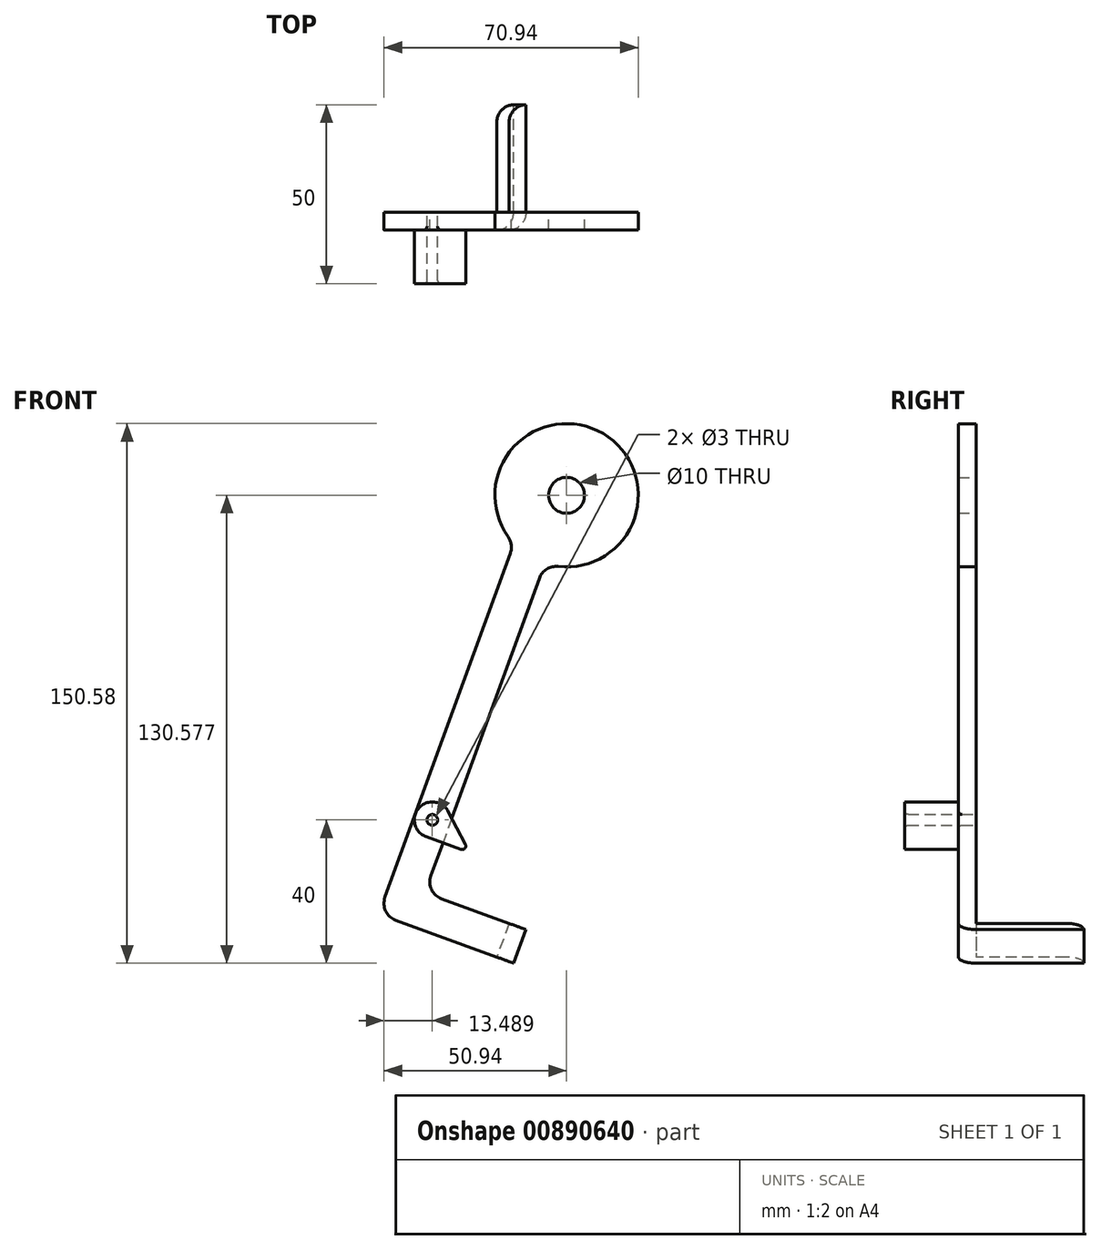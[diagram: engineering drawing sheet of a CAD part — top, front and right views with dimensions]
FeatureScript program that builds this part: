
annotation { "Feature Type Name" : "Feature", "Feature Type Description" : "" }
export const myFeature = defineFeature(function(context is Context, id is Id, definition is map)
    precondition{}
    {
        {
            var Q0;
            Q0=qCreatedBy(makeId("Front.planeOp"),FACE);
            var sketch = newSketch(context, id + "F0", { "sketchPlane" : qUnion([Q0])});
            skCircle(sketch, "E0", {"center": v(0, 33.82) * mm, "radius": 5 * mm});
            skLineSegment(sketch, "E1", {"start": v(0, 70.54) * mm, "end": v(0, -41.15) * mm, "construction": true});
            skLineSegment(sketch, "E2", {"start": v(-33.6, -60.82) * mm, "end": v(-32.58, -58) * mm});
            skLineSegment(sketch, "E3", {"start": v(-32.58, -58) * mm, "end": v(-32.58, -58) * mm});
            skCircle(sketch, "E4", {"center": v(0, 33.82) * mm, "radius": 20 * mm});
            skLineSegment(sketch, "E5", {"start": v(-6.1, 14.77) * mm, "end": v(-32.58, -58) * mm});
            skLineSegment(sketch, "E6", {"start": v(-14.73, 20.29) * mm, "end": v(-42.32, -55.52) * mm});
            skLineSegment(sketch, "E7", {"start": v(-14.73, 20.29) * mm, "end": v(-52.35, -83.08) * mm});
            skLineSegment(sketch, "E8", {"start": v(-6.1, 14.77) * mm, "end": v(-42.95, -86.5) * mm});
            skLineSegment(sketch, "E9", {"start": v(-52.35, -83.08) * mm, "end": v(-42.95, -86.5) * mm});
            skLineSegment(sketch, "E10", {"start": v(-42.95, -86.5) * mm, "end": v(-14.76, -96.76) * mm});
            skLineSegment(sketch, "E11", {"start": v(-14.76, -96.76) * mm, "end": v(-11.34, -87.36) * mm});
            skLineSegment(sketch, "E12", {"start": v(-11.34, -87.36) * mm, "end": v(-39.53, -77.1) * mm});
            skLineSegment(sketch, "E13", {"start": v(-16.04, -85.65) * mm, "end": v(-19.46, -95.05) * mm});
            skCircle(sketch, "E14", {"center": v(-37.45, -56.76) * mm, "radius": 5 * mm});
            skCircle(sketch, "E15", {"center": v(-37.45, -56.76) * mm, "radius": 1.5 * mm});
            skLineSegment(sketch, "E16", {"start": v(-37.45, -56.76) * mm, "end": v(-36.77, -54.88) * mm, "construction": true});
            skLineSegment(sketch, "E17", {"start": v(-37.45, -56.76) * mm, "end": v(-38.14, -58.64) * mm, "construction": true});
            skLineSegment(sketch, "E18", {"start": v(-36.77, -54.88) * mm, "end": v(-32.07, -56.6) * mm, "construction": true});
            skLineSegment(sketch, "E19", {"start": v(-38.14, -58.64) * mm, "end": v(-33.44, -60.35) * mm, "construction": true});
            skLineSegment(sketch, "E20", {"start": v(-33.83, -60.2) * mm, "end": v(-33.44, -60.35) * mm});
            skLineSegment(sketch, "E21", {"start": v(-32.46, -56.45) * mm, "end": v(-32.07, -56.6) * mm});
            skLineSegment(sketch, "E22", {"start": v(-32.07, -56.6) * mm, "end": v(-24.55, -59.33) * mm});
            skLineSegment(sketch, "E23", {"start": v(-33.44, -60.35) * mm, "end": v(-25.92, -63.09) * mm});
            skLineSegment(sketch, "E24", {"start": v(-24.55, -59.33) * mm, "end": v(-25.92, -63.09) * mm});
            skLineSegment(sketch, "E25", {"start": v(-32.07, -56.6) * mm, "end": v(-30.66, -57.1) * mm});
            skLineSegment(sketch, "E26", {"start": v(-30.66, -57.1) * mm, "end": v(-32.03, -60.86) * mm});
            skLineSegment(sketch, "E27", {"start": v(-30.66, -57.1) * mm, "end": v(-25.92, -63.09) * mm});
            skSolve(sketch);
        }
        {
            var Q0;
            Q0=makeQuery(id+"F0.imprint","IMPRINT",FACE,{"disambiguationData":[TD([[makeQuery(id+"F0.imprint","IMPRINT",EDGE,{"derivedFrom":sQuery(id+"F0.wireOp",EDGE,"E0")}),-1.0]])]});
            var Q1;
            {var subQ3=sQuery(id+"F0.wireOp",EDGE,"E21");Q1=makeQuery(id+"F0.imprint","IMPRINT",FACE,{"disambiguationData":[TD([[makeQuery(id+"F0.imprint","IMPRINT",EDGE,{"derivedFrom":subQ3}),1.0]])]});}
            var Q2;
            {var subQ0=sQuery(id+"F0.wireOp",EDGE,"E21");Q2=makeQuery(id+"F0.imprint","IMPRINT",FACE,{"disambiguationData":[TD([[makeQuery(id+"F0.imprint","IMPRINT",EDGE,{"derivedFrom":subQ0}),-1.0]])]});}
            var Q3;
            Q3=makeQuery(id+"F0.imprint","IMPRINT",FACE,{"disambiguationData":[TD([[makeQuery(id+"F0.imprint","IMPRINT",EDGE,{"derivedFrom":sQuery(id+"F0.wireOp",EDGE,"E15")}),-1.0]])]});
            var Q4;
            {var subQ0=sQuery(id+"F0.wireOp",EDGE,"E9");Q4=makeQuery(id+"F0.imprint","IMPRINT",FACE,{"disambiguationData":[TD([[makeQuery(id+"F0.imprint","IMPRINT",EDGE,{"derivedFrom":subQ0}),1.0]])]});}
            var Q5;
            {var subQ0=sQuery(id+"F0.wireOp",EDGE,"E20");Q5=makeQuery(id+"F0.imprint","IMPRINT",FACE,{"disambiguationData":[TD([[makeQuery(id+"F0.imprint","IMPRINT",EDGE,{"derivedFrom":subQ0}),1.0]])]});}
            var Q6;
            {var subQ5=sQuery(id+"F0.wireOp",EDGE,"E13");Q6=makeQuery(id+"F0.imprint","IMPRINT",FACE,{"disambiguationData":[TD([[makeQuery(id+"F0.imprint","IMPRINT",EDGE,{"derivedFrom":subQ5}),-1.0]])]});}
            var Q7;
            {var subQ0=sQuery(id+"F0.wireOp",EDGE,"E11");Q7=makeQuery(id+"F0.imprint","IMPRINT",FACE,{"disambiguationData":[TD([[makeQuery(id+"F0.imprint","IMPRINT",EDGE,{"derivedFrom":subQ0}),1.0]])]});}
            extrude(context, id + "F1", {"entities" : qUnion([Q0, Q1, Q2, Q3, Q4, Q5, Q6, Q7]), "depth" : 5 * mm, "offsetDistance" : 25 * mm});
        }
        {
            var Q0;
            {var subQ0=sQuery(id+"F0.wireOp",EDGE,"E11");Q0=makeQuery(id+"F0.imprint","IMPRINT",FACE,{"disambiguationData":[TD([[makeQuery(id+"F0.imprint","IMPRINT",EDGE,{"derivedFrom":subQ0}),1.0]])]});}
            extrude(context, id + "F2", {"entities" : qUnion([Q0]), "operationType" : NewBodyOperationType.ADD, "oppositeDirection" : true, "depth" : 30 * mm, "offsetDistance" : 25 * mm});
        }
        {
            var Q0;
            Q0=makeQuery(id+"F1.opExtrude","CAP_FACE",FACE,{"disambiguationData":[OSD([sQuery(id+"F0.wireOp",EDGE,"E0"),sQuery(id+"F0.wireOp",EDGE,"E4"),sQuery(id+"F0.wireOp",EDGE,"E7"),sQuery(id+"F0.wireOp",EDGE,"E8"),sQuery(id+"F0.wireOp",EDGE,"E9"),sQuery(id+"F0.wireOp",EDGE,"E10"),sQuery(id+"F0.wireOp",EDGE,"E11"),sQuery(id+"F0.wireOp",EDGE,"E12"),sQuery(id+"F0.wireOp",EDGE,"E15")])],"isStart":false});
            var sketch = newSketch(context, id + "F3", { "sketchPlane" : qUnion([Q0])});
            skCircle(sketch, "E28.0", {"center": v(-37.45, -56.76) * mm, "radius": 5 * mm});
            skCircle(sketch, "E28.1", {"center": v(-37.45, -56.76) * mm, "radius": 1.5 * mm});
            skLineSegment(sketch, "E28.4", {"start": v(-6.1, 14.77) * mm, "end": v(-42.95, -86.5) * mm});
            skLineSegment(sketch, "E29", {"start": v(-37.45, -56.76) * mm, "end": v(-39.16, -61.46) * mm, "construction": true});
            skLineSegment(sketch, "E30", {"start": v(-39.16, -61.46) * mm, "end": v(-27.03, -65.88) * mm});
            skLineSegment(sketch, "E31", {"start": v(-27.03, -65.88) * mm, "end": v(-33.02, -54.44) * mm});
            skSolve(sketch);
        }
        {
            var Q0;
            Q0=makeQuery(id+"F1.opExtrude","SWEPT_EDGE",EDGE,{"disambiguationData":[OSD([sQuery(id+"F0.wireOp",EDGE,"E7"),sQuery(id+"F0.wireOp",EDGE,"E9")])]});
            var Q1;
            Q1=makeQuery(id+"F1.opExtrude","CAP_EDGE",EDGE,{"disambiguationData":[OSD([sQuery(id+"F0.wireOp",EDGE,"E11")])],"isStart":false});
            var Q2;
            Q2=makeQuery(id+"F2.opExtrude","CAP_EDGE",EDGE,{"disambiguationData":[OSD([sQuery(id+"F0.wireOp",EDGE,"E13")])],"isStart":false});
            var Q3;
            Q3=makeQuery(id+"F2.opExtrude","CAP_EDGE",EDGE,{"disambiguationData":[OSD([sQuery(id+"F0.wireOp",EDGE,"E13")])],"isStart":true});
            var Q4;
            Q4=makeQuery(id+"F1.opExtrude","SWEPT_EDGE",EDGE,{"disambiguationData":[OSD([sQuery(id+"F0.wireOp",EDGE,"E8"),sQuery(id+"F0.wireOp",EDGE,"E12")])]});
            fillet(context, id + "F4", {"entities" : qUnion([Q0, Q1, Q2, Q3, Q4]), "radius" : 5 * mm, "tangentPropagation" : true, "allowEdgeOverflow" : false});
        }
        {
            var Q0;
            Q0=makeQuery(id+"F1.opExtrude","SWEPT_EDGE",EDGE,{"disambiguationData":[OSD([sQuery(id+"F0.wireOp",EDGE,"E4"),sQuery(id+"F0.wireOp",EDGE,"E8")])]});
            var Q1;
            Q1=makeQuery(id+"F1.opExtrude","SWEPT_EDGE",EDGE,{"disambiguationData":[OSD([sQuery(id+"F0.wireOp",EDGE,"E4"),sQuery(id+"F0.wireOp",EDGE,"E7")])]});
            fillet(context, id + "F5", {"entities" : qUnion([Q0, Q1]), "radius" : 5 * mm, "tangentPropagation" : true, "allowEdgeOverflow" : false});
        }
        {
            var Q0;
            {var subQ0=sQuery(id+"F3.wireOp",EDGE,"QKELsI9O-PcXz-MsMN-dyrf-KZIwZTE5pGb1");Q0=makeQuery(id+"F3.imprint","IMPRINT",FACE,{"disambiguationData":[TD([[makeQuery(id+"F3.imprint","IMPRINT",EDGE,{"derivedFrom":subQ0}),-1.0]])]});}
            var Q1;
            {var subQ0=sQuery(id+"F3.wireOp",EDGE,"nzNBqJ3v-BiOq-ahzX-1OQT-qNi1GnngYHaL");var subQ1=sQuery(id+"F3.wireOp",EDGE,"E28.0");var subQ2=makeQuery(id+"F3.imprint","INTERSECT",VERTEX,{"derivedFrom":[subQ1,subQ0]});Q1=makeQuery(id+"F3.imprint","IMPRINT",FACE,{"disambiguationData":[TD([[makeQuery(id+"F3.imprint","IMPRINT",EDGE,{"disambiguationData":[TD([[subQ2,1.0]])],"derivedFrom":subQ1}),-1.0]])]});}
            var Q2;
            Q2=makeQuery(id+"F3.imprint","IMPRINT",FACE,{"disambiguationData":[TD([[makeQuery(id+"F3.imprint","IMPRINT",EDGE,{"derivedFrom":sQuery(id+"F3.wireOp",EDGE,"E28.1")}),-1.0]])]});
            var Q3;
            {var subQ0=sQuery(id+"F3.wireOp",EDGE,"E30");var subQ1=sQuery(id+"F3.wireOp",EDGE,"E28.0");var subQ2=makeQuery(id+"F3.imprint","INTERSECT",VERTEX,{"derivedFrom":[subQ1,subQ0]});Q3=makeQuery(id+"F3.imprint","IMPRINT",FACE,{"disambiguationData":[TD([[makeQuery(id+"F3.imprint","IMPRINT",EDGE,{"disambiguationData":[TD([[subQ2,-1.0]])],"derivedFrom":subQ1}),-1.0]])]});}
            var Q4;
            {var subQ0=sQuery(id+"F3.wireOp",EDGE,"E31");var subQ1=sQuery(id+"F3.wireOp",EDGE,"E28.4");var subQ2=makeQuery(id+"F3.imprint","INTERSECT",VERTEX,{"derivedFrom":[subQ1,subQ0]});Q4=makeQuery(id+"F3.imprint","IMPRINT",FACE,{"disambiguationData":[TD([[makeQuery(id+"F3.imprint","IMPRINT",EDGE,{"disambiguationData":[TD([[subQ2,-1.0]])],"derivedFrom":subQ1}),1.0]])]});}
            extrude(context, id + "F6", {"entities" : qUnion([Q0, Q1, Q2, Q3, Q4]), "depth" : 15 * mm, "offsetDistance" : 25 * mm});
        }
        {
            var Q0;
            Q0=makeQuery(id+"F6.opExtrude","SWEPT_EDGE",EDGE,{"disambiguationData":[OSD([sQuery(id+"F3.wireOp",EDGE,"E30"),sQuery(id+"F3.wireOp",EDGE,"E31")])]});
            var Q1;
            Q1=makeQuery(id+"F6.opExtrude","CAP_EDGE",EDGE,{"disambiguationData":[OSD([sQuery(id+"F3.wireOp",EDGE,"E28.1")])],"isStart":false});
            var Q2;
            Q2=makeQuery(id+"F1.opExtrude","CAP_EDGE",EDGE,{"disambiguationData":[OSD([sQuery(id+"F0.wireOp",EDGE,"E15")])],"isStart":false});
            fillet(context, id + "F7", {"entities" : qUnion([Q0, Q1, Q2]), "radius" : 1 * mm, "tangentPropagation" : true, "allowEdgeOverflow" : false});
        }
    });
